# Revit family: Shower-Button_Interface-KOHLER-K-28213
name_source: partatom
category: Specialty Equipment
revit_build: Autodesk Revit 2017 (Build: 20160225_1515(x64)
units: mm (PartAtom-declared; Revit-internal decimal feet)

## family parameters
Cut with Voids When Loaded = No
Host = Face
OmniClass Number = 23.31.25.00
OmniClass Title = Toilet and Bath Specialties
Part Type = Normal
Room Calculation Point = No
Round Connector Dimension = Use Diameter
Shared = No

## types (5) — shared parameters
ADA Compliant = No
Assembly Code = C1030200
Date Modified = 02/25/2021
Default Elevation = 42"
Description = REMOTE ON/OFF INTERFACE
Height = 2 1/4"
Length = 1"
Manufacturer = KOHLER Co.
Master Format 2014 = 10 28 00
Master Format 2014 Name = Toilet, Bath, and Laundry Accessories
Material = Plastic
Product Documentation Link = https://www.us.kohler.com
Product Page URL = http://www.us.kohler.com
URL = https://www.us.kohler.com
WaterSense Certified = No
Width = 2 1/4"

## per-type parameters (varying)
| type | Finish | Model | Type |
| CP-Polished Chrome | Kohler-Plastic-CP-Polished_Chrome | K-28213-CP | 1 |
| BN-Vibrant Brushed Nickel | KOHLER-Plastic-BN-Vibrant_Brushed_Nickel | K-28213-BN | 2 |
| BL-Matte Black | Kohler-Plactic-BL-Matte_Black | K-28213-BL | 3 |
| SN-Vibrant Polished Nickel | KOHLER-Plasticl-SN-Vibrant_Polished_Nickel | K-28213-SN | 4 |
| 2MB-Vibrant Brushed Moderne Brass | Kohler-Plastic-2MB-Vibrant_Brushed_Moderne_Brass | K-28213-2MB | 5 |

## geometry (parser evidence)
native form markers: Sweep x4
no freeform markers — native parametric forms only
